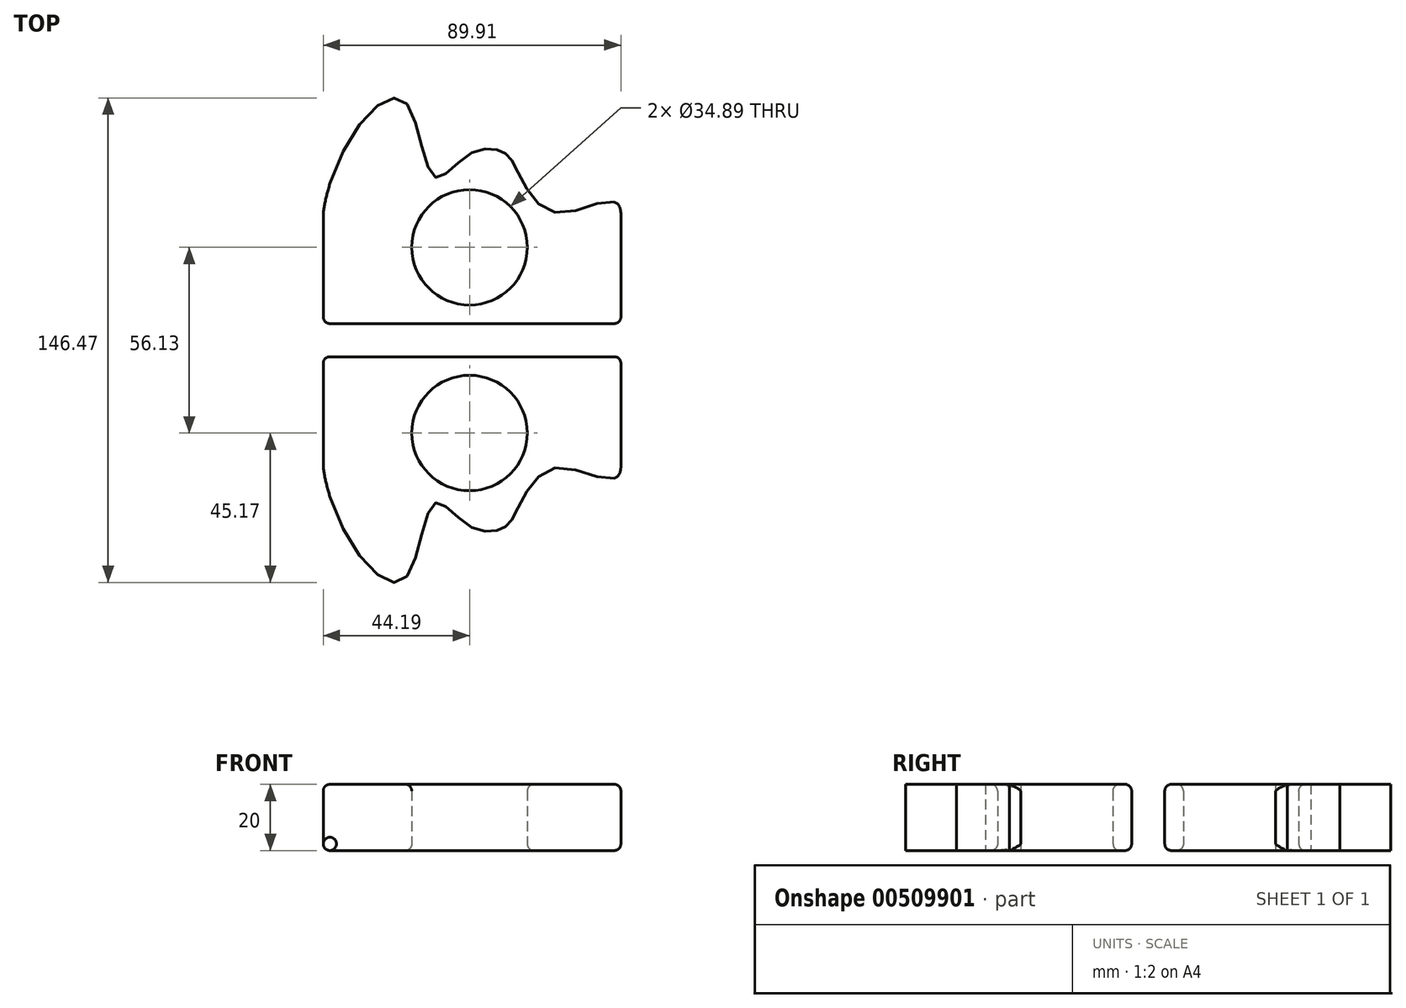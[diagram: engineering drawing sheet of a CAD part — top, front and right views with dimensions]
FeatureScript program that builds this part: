
annotation { "Feature Type Name" : "Feature", "Feature Type Description" : "" }
export const myFeature = defineFeature(function(context is Context, id is Id, definition is map)
    precondition{}
    {
        {
            var Q0;
            Q0=qCreatedBy(makeId("Top.planeOp"),FACE);
            var sketch = newSketch(context, id + "F0", { "sketchPlane" : qUnion([Q0])});
            skLineSegment(sketch, "E0", {"start": v(-44.2, 0) * mm, "end": v(-44.2, 33.46) * mm});
            skLineSegment(sketch, "E1", {"start": v(-44.2, 33.46) * mm, "end": v(45.72, 33.46) * mm});
            skLineSegment(sketch, "E2", {"start": v(45.72, 33.46) * mm, "end": v(45.72, 0) * mm});
            skFitSpline(sketch, "E3", {"points": [v(-44.2, 0) * mm, v(-20.3, -34.17) * mm, v(-10.75, -10.94) * mm, v(0, -17.77) * mm, v(9.52, -18.64) * mm, v(13.6, -14.21) * mm, v(27.16, 0) * mm, v(45.72, 0) * mm], "startDerivative": vector(36.19, -260.46) * mm, "endDerivative": vector(12.5, 164.1) * mm});
            skCircle(sketch, "E4", {"center": v(0, 10.4) * mm, "radius": 17.44 * mm});
            skSolve(sketch);
        }
        {
            var Q0;
            Q0 = qSketchRegion(id + "F0", true);
            extrude(context, id + "F1", {"entities" : qUnion([Q0]), "depth" : 20 * mm});
        }
        {
            var Q0;
            Q0=makeQuery(id+"F1.opExtrude","CAP_EDGE",EDGE,{"disambiguationData":[OSD([sQuery(id+"F0.wireOp",EDGE,"E2")])],"isStart":false});
            var Q1;
            Q1=makeQuery(id+"F1.opExtrude","CAP_EDGE",EDGE,{"disambiguationData":[OSD([sQuery(id+"F0.wireOp",EDGE,"E2")])],"isStart":true});
            var Q2;
            Q2=makeQuery(id+"F1.opExtrude","CAP_EDGE",EDGE,{"disambiguationData":[OSD([sQuery(id+"F0.wireOp",EDGE,"E0")])],"isStart":false});
            var Q3;
            Q3=makeQuery(id+"F1.opExtrude","CAP_EDGE",EDGE,{"disambiguationData":[OSD([sQuery(id+"F0.wireOp",EDGE,"E0")])],"isStart":true});
            var Q4;
            Q4=makeQuery(id+"F1.opExtrude","SWEPT_EDGE",EDGE,{"disambiguationData":[OSD([sQuery(id+"F0.wireOp",EDGE,"E0"),sQuery(id+"F0.wireOp",EDGE,"E1")])]});
            var Q5;
            Q5=makeQuery(id+"F1.opExtrude","SWEPT_EDGE",EDGE,{"disambiguationData":[OSD([sQuery(id+"F0.wireOp",EDGE,"E1"),sQuery(id+"F0.wireOp",EDGE,"E2")])]});
            var Q6;
            Q6=makeQuery(id+"F1.opExtrude","CAP_EDGE",EDGE,{"disambiguationData":[OSD([sQuery(id+"F0.wireOp",EDGE,"E1")])],"isStart":true});
            var Q7;
            Q7=makeQuery(id+"F1.opExtrude","SWEPT_FACE",FACE,{"disambiguationData":[OSD([sQuery(id+"F0.wireOp",EDGE,"E1")])]});
            var Q8;
            Q8=makeQuery(id+"F1.opExtrude","CAP_EDGE",EDGE,{"disambiguationData":[OSD([sQuery(id+"F0.wireOp",EDGE,"E4")])],"isStart":true});
            var Q9;
            Q9=makeQuery(id+"F1.opExtrude","CAP_EDGE",EDGE,{"disambiguationData":[OSD([sQuery(id+"F0.wireOp",EDGE,"E4")])],"isStart":false});
            fillet(context, id + "F2", {"entities" : qUnion([Q0, Q1, Q2, Q3, Q4, Q5, Q6, Q7, Q8, Q9]), "radius" : 2 * mm, "tangentPropagation" : true, "allowEdgeOverflow" : false});
        }
        {
            var Q0;
            Q0=makeQuery(id+"F1.opExtrude","SWEPT_BODY",BODY,{"disambiguationData":[OSD([sQuery(id+"F0.wireOp",EDGE,"E0"),sQuery(id+"F0.wireOp",EDGE,"E1"),sQuery(id+"F0.wireOp",EDGE,"E2"),sQuery(id+"F0.wireOp",EDGE,"E3"),sQuery(id+"F0.wireOp",EDGE,"E4")])]});
            var Q1;
            Q1=makeQuery(id+"F1.opExtrude","SWEPT_FACE",FACE,{"disambiguationData":[OSD([sQuery(id+"F0.wireOp",EDGE,"E1")])]});
            mirror(context, id + "F3", {"entities" : qUnion([Q0]), "mirrorPlane" : qUnion([Q1])});
        }
        {
            var Q0;
            Q0=makeQuery(id+"F3.opPattern","COPY",BODY,{"derivedFrom":makeQuery(id+"F1.opExtrude","SWEPT_BODY",BODY,{"disambiguationData":[OSD([sQuery(id+"F0.wireOp",EDGE,"E0"),sQuery(id+"F0.wireOp",EDGE,"E1"),sQuery(id+"F0.wireOp",EDGE,"E2"),sQuery(id+"F0.wireOp",EDGE,"E3"),sQuery(id+"F0.wireOp",EDGE,"E4")])]}),"instanceName":"1"});
            var Q1;
            Q1=qCreatedBy(makeId("Front.planeOp"),FACE);
            transform(context, id + "F4", {"entities" : qUnion([Q0]), "transformType" : TransformType.TRANSLATION_DISTANCE, "transformDirection" : qUnion([Q1]), "distance" : 10 * mm, "oppositeDirection" : true, "makeCopy" : false});
        }
    });
